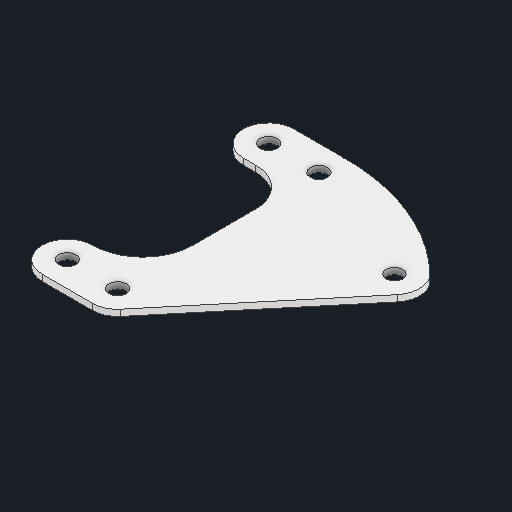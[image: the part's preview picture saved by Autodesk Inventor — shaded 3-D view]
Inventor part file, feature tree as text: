
AUTODESK INVENTOR PART (.ipt)
format: ipt  version: 2025 (Build 290162000, 162)  size: 169,984 bytes
history: native  units: in
note: dims shown in document units (in); Inventor stores cm internally (conversion verified against a paired STEP export)
features: other x4, extrude x1, sketch x1
ambient origin geometry x8: Origin, YZ Plane, XZ Plane, XY Plane, X Axis, Y Axis, Z Axis, Center Point
bodies: Solid1 (feature_tree)
feature tree (6):
  other  "Blocks"
  extrude  "Extrusion1"  Depth=0.5in
  sketch  "Sketch1"  dims[d0=0.5in d1=0.5in d2=0.375in d3=0.0625in d4=0.0in]
  other  "main"
  other  "main:1"
  other  "Definition1"
